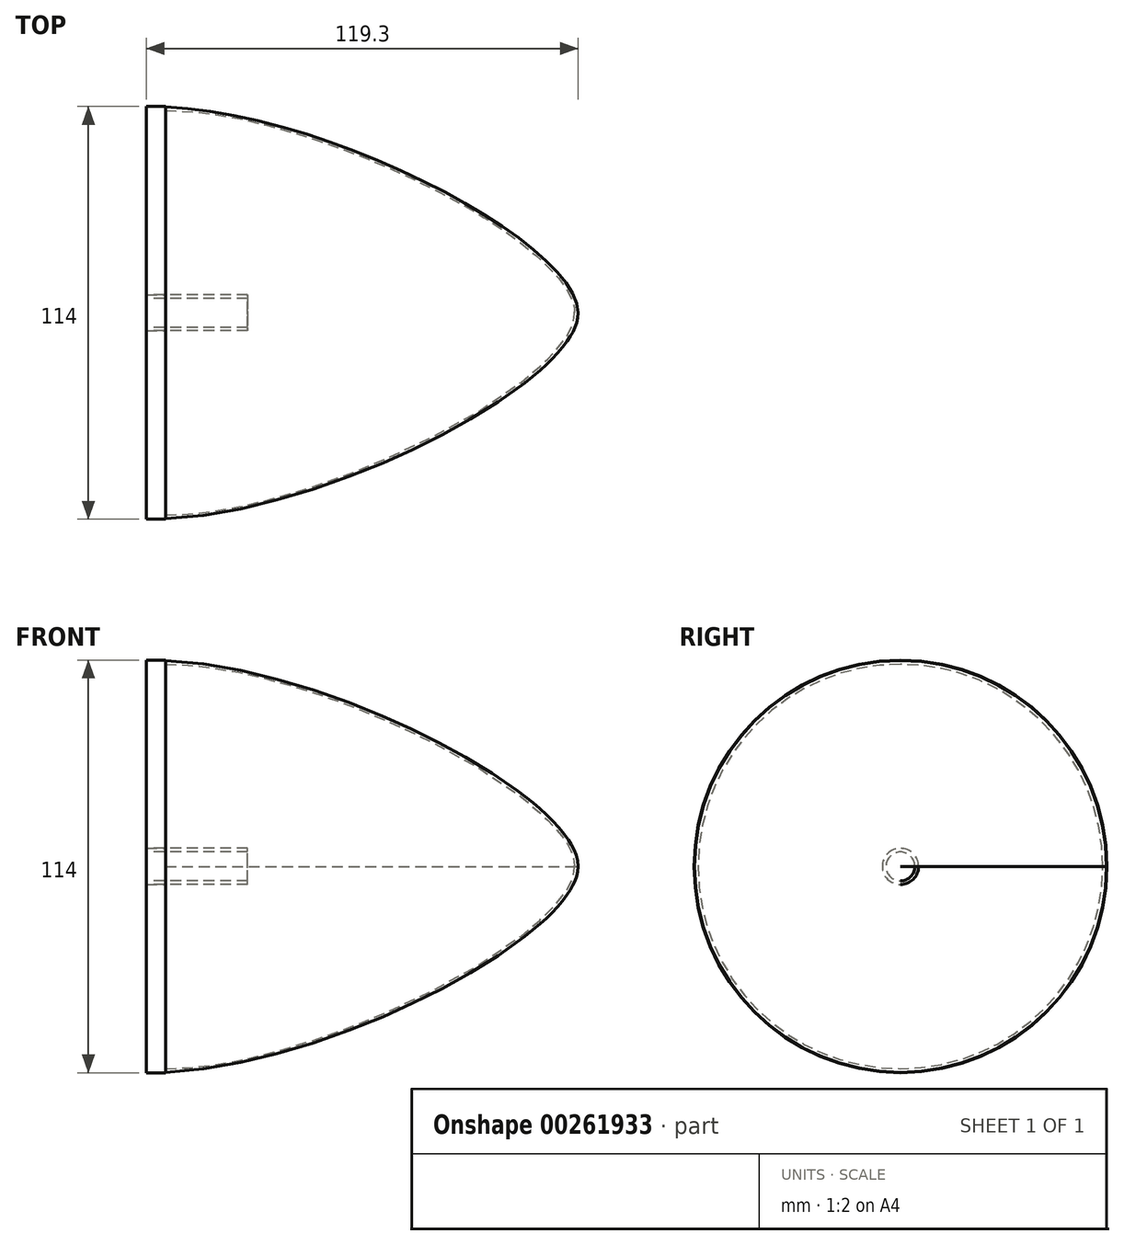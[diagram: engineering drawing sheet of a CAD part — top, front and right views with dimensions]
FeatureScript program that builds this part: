
annotation { "Feature Type Name" : "Feature", "Feature Type Description" : "" }
export const myFeature = defineFeature(function(context is Context, id is Id, definition is map)
    precondition{}
    {
        {
            var Q0;
            Q0=qCreatedBy(makeId("Right.planeOp"),FACE);
            var sketch = newSketch(context, id + "F0", { "sketchPlane" : qUnion([Q0])});
            skCircle(sketch, "E0", {"center": v(0, 0) * mm, "radius": 57 * mm});
            skCircle(sketch, "E1", {"center": v(0, 0) * mm, "radius": 5 * mm});
            skCircle(sketch, "E2", {"center": v(0, 0) * mm, "radius": 4 * mm});
            skCircle(sketch, "E3", {"center": v(0, 0) * mm, "radius": 22.5 * mm});
            skLineSegment(sketch, "E4", {"start": v(0, 0) * mm, "end": v(254, 0) * mm, "construction": true});
            skLineSegment(sketch, "E5", {"start": v(0, 22.5) * mm, "end": v(0, -22.5) * mm, "construction": true});
            skFitSpline(sketch, "E6", {"points": [v(0, 22.5) * mm, v(22.76, 17.06) * mm, v(254, 0) * mm], "startDerivative": vector(118.12, 0) * mm, "endDerivative": vector(-2.2, -90.77) * mm});
            skFitSpline(sketch, "E7.MirrorCS", {"points": [v(0, -22.5) * mm, v(22.76, -17.06) * mm, v(254, 0) * mm], "startDerivative": vector(118.12, 0) * mm, "endDerivative": vector(-2.2, 90.77) * mm});
            skFitSpline(sketch, "E8.MirrorCS", {"points": [v(0, 22.5) * mm, v(-22.76, 17.06) * mm, v(-254, 0) * mm], "startDerivative": vector(-118.12, 0) * mm, "endDerivative": vector(2.2, -90.77) * mm});
            skFitSpline(sketch, "E9.MirrorCS", {"points": [v(0, -22.5) * mm, v(-22.76, -17.06) * mm, v(-254, 0) * mm], "startDerivative": vector(-118.12, 0) * mm, "endDerivative": vector(2.2, 90.77) * mm});
            skLineSegment(sketch, "E10", {"start": v(0, 22.5) * mm, "end": v(-24.5, 22.5) * mm, "construction": true});
            skPoint(sketch, "E11", {"position": v(22.5, 0) * mm});
            skPoint(sketch, "E12", {"position": v(57, 0) * mm});
            skPoint(sketch, "E13", {"position": v(244, 0) * mm});
            skPoint(sketch, "E14", {"position": v(127, 0) * mm});
            skPoint(sketch, "E15", {"position": v(22.5, -17.1) * mm});
            skPoint(sketch, "E16", {"position": v(22.5, 17.1) * mm});
            skPoint(sketch, "E17", {"position": v(57, -15.35) * mm});
            skPoint(sketch, "E18", {"position": v(57, 15.35) * mm});
            skPoint(sketch, "E19", {"position": v(127, 15.16) * mm});
            skPoint(sketch, "E20", {"position": v(127, -15.16) * mm});
            skPoint(sketch, "E21", {"position": v(244, 7.77) * mm});
            skPoint(sketch, "E22", {"position": v(244, -7.77) * mm});
            skSolve(sketch);
        }
        {
            var Q0;
            {var subQ0=sQuery(id+"F0.wireOp",EDGE,"E8.MirrorCS");var subQ1=sQuery(id+"F0.wireOp",EDGE,"E0");var subQ2=makeQuery(id+"F0.imprint","INTERSECT",VERTEX,{"derivedFrom":[subQ1,subQ0]});Q0=makeQuery(id+"F0.imprint","IMPRINT",FACE,{"disambiguationData":[TD([[makeQuery(id+"F0.imprint","IMPRINT",EDGE,{"disambiguationData":[TD([[subQ2,1.0]])],"derivedFrom":subQ1}),1.0]])]});}
            var Q1;
            {var subQ0=sQuery(id+"F0.wireOp",EDGE,"E8.MirrorCS");var subQ1=sQuery(id+"F0.wireOp",EDGE,"E0");var subQ2=makeQuery(id+"F0.imprint","INTERSECT",VERTEX,{"derivedFrom":[subQ1,subQ0]});Q1=makeQuery(id+"F0.imprint","IMPRINT",FACE,{"disambiguationData":[TD([[makeQuery(id+"F0.imprint","IMPRINT",EDGE,{"disambiguationData":[TD([[subQ2,-1.0]])],"derivedFrom":subQ1}),1.0]])]});}
            var Q2;
            {var subQ0=sQuery(id+"F0.wireOp",EDGE,"E9.MirrorCS");var subQ1=sQuery(id+"F0.wireOp",EDGE,"E0");var subQ2=makeQuery(id+"F0.imprint","INTERSECT",VERTEX,{"derivedFrom":[subQ1,subQ0]});Q2=makeQuery(id+"F0.imprint","IMPRINT",FACE,{"disambiguationData":[TD([[makeQuery(id+"F0.imprint","IMPRINT",EDGE,{"disambiguationData":[TD([[subQ2,-1.0]])],"derivedFrom":subQ1}),1.0]])]});}
            var Q3;
            {var subQ0=sQuery(id+"F0.wireOp",EDGE,"E6");var subQ1=sQuery(id+"F0.wireOp",EDGE,"E0");var subQ2=makeQuery(id+"F0.imprint","INTERSECT",VERTEX,{"derivedFrom":[subQ1,subQ0]});Q3=makeQuery(id+"F0.imprint","IMPRINT",FACE,{"disambiguationData":[TD([[makeQuery(id+"F0.imprint","IMPRINT",EDGE,{"disambiguationData":[TD([[subQ2,1.0]])],"derivedFrom":subQ1}),1.0]])]});}
            var Q4;
            Q4=makeQuery(id+"F0.imprint","IMPRINT",FACE,{"disambiguationData":[TD([[makeQuery(id+"F0.imprint","IMPRINT",EDGE,{"derivedFrom":sQuery(id+"F0.wireOp",EDGE,"E1")}),-1.0]])]});
            extrude(context, id + "F1", {"entities" : qUnion([Q0, Q1, Q2, Q3, Q4]), "oppositeDirection" : true, "depth" : 5.3 * mm});
        }
        {
            var Q0;
            Q0=makeQuery(id+"F0.imprint","IMPRINT",FACE,{"disambiguationData":[TD([[makeQuery(id+"F0.imprint","IMPRINT",EDGE,{"derivedFrom":sQuery(id+"F0.wireOp",EDGE,"E1")}),1.0]])]});
            extrude(context, id + "F2", {"entities" : qUnion([Q0]), "depth" : 22.7 * mm, "hasSecondDirection" : true, "secondDirectionOppositeDirection" : true, "secondDirectionDepth" : 5.3 * mm});
        }
        {
            var Q0;
            Q0=qCreatedBy(makeId("Top.planeOp"),FACE);
            var sketch = newSketch(context, id + "F3", { "sketchPlane" : qUnion([Q0])});
            skLineSegment(sketch, "E23.0", {"start": v(-5.3, -57) * mm, "end": v(-5.3, 57) * mm});
            skLineSegment(sketch, "E24", {"start": v(-5.3, 0) * mm, "end": v(114, 0) * mm, "construction": true});
            skFitSpline(sketch, "E25", {"points": [v(0, 56.87) * mm, v(114, 0) * mm], "startDerivative": vector(137.81, -5.43) * mm, "endDerivative": vector(0.33, -57.1) * mm});
            skFitSpline(sketch, "E26.0", {"points": [v(-0.04, 55.87) * mm, v(5.64, 55.65) * mm, v(17.72, 54.14) * mm, v(36.89, 49.27) * mm, v(56.03, 42.4) * mm, v(74.09, 34.13) * mm, v(90, 25.07) * mm, v(100.56, 17.36) * mm, v(106.85, 11.44) * mm, v(110.36, 7.2) * mm, v(112.16, 3.96) * mm, v(112.87, 1.6) * mm, v(113, 0.51) * mm, v(113, 0) * mm]});
            skLineSegment(sketch, "E27", {"start": v(113, 0) * mm, "end": v(114, 0) * mm});
            skLineSegment(sketch, "E28", {"start": v(0, 55.87) * mm, "end": v(0, 56.87) * mm});
            skSolve(sketch);
        }
        {
            var Q0;
            Q0=makeQuery(id+"F3.imprint","IMPRINT",FACE,{"disambiguationData":[TD([[makeQuery(id+"F3.imprint","IMPRINT",EDGE,{"derivedFrom":sQuery(id+"F3.wireOp",EDGE,"E25")}),-1.0]])]});
            var Q1;
            Q1=sQuery(id+"F3.wireOp",EDGE,"E24");
            revolve(context, id + "F4", {"surfaceOperationType" : NewSurfaceOperationType.NEW, "entities" : qUnion([Q0]), "axis" : qUnion([Q1]), "revolveType" : RevolveType.FULL});
        }
        {
            var Q0;
            Q0=qCreatedBy(makeId("Front.planeOp"),FACE);
            var Q1;
            Q1=sQuery(id+"F0.wireOp",VERTEX,"E11");
            cPlane(context, id + "F5", {"entities" : qUnion([Q0, Q1]), "cplaneType" : CPlaneType.PLANE_POINT, "offset" : 25 * mm, "width" : 150 * mm, "height" : 150 * mm});
        }
    });
